# Revit family: 2CKA002064A0301
name_source: partatom
category: Elektroinstallationen
revit_build: Autodesk Revit 2017 (Build: 20160225_1515(x64)
units: mm (PartAtom-declared; Revit-internal decimal feet)

## family parameters
Basisbauteil = Fläche
Beim Laden mit Abzugskörper schneiden = Nein
Bemaßung runder Anschluss = Durchmesser verwenden
Beschriftungsausrichtung beibehalten = Ja
Gemeinsam genutzt = Nein
Raumberechnungspunkt = Nein
Teiletyp = Normal

## types (1)
- 2CKA002064A0301
    Abschließbar = Nein
    Anschlussart = Steckklemme
    Anzahl der Einheiten = 1
    Aufdruck/Kennzeichnung = ohne Aufdruck
    Ausführung = Schuko
    Ausführung der Oberfläche = glänzend
    Auswurfmechanismus = Nein
    BIM = https://media.live.bim.site
    BIMSITE_PRODUCT_ID = db384c0cd55333414ae2b7e2fc57784a7c25efdb
    Befestigungsart = Krallen-/Schraubbefestigung
    Beschreibung = SCHUKO Steckdosen-Einsatz, alpinweiß, Unterputz wassergeschützt, Sondersteckvorrichtungen, Steckdosen, SCHUKO Steckdosen-Einsatz mit Klappdeckel und Beschriftungsfeld Beschriftungsfeld 66,7 x 10 mm. Mit erhöhtem Berührungsschutz. Lieferumfang mit Dichtungsring. IP 44 nur in Verbindung mit Rahmen Allwetter 44. Mit Steckanschluss. 2-polig (2 P + E) Nennstrom: 16 A Schutzart Gerät: IP 44
    Datenblatt = https://media.live.bim.site
    Farbe = weiß
    Fehlerstromschutz = Nein
    GTIN = 4011395172322
    Geeignet für Schutzart (IP) = IP44
    Gerätebreite [mm] = 70
    Gerätehöhe [mm] = 131
    Gewicht [kg/m] = 0.097
    HAN = 2CKA002064A0301
    Halogenfrei = Ja
    HeinzeBIM = https://www.heinze.de
    Hersteller = Busch-Jaeger
    Ist System = Nein
    Ist Zubehör = Nein
    Metal = Metal
    Mit Klappdeckel = Ja
    Mit erhöhtem Berührungsschutz = Ja
    Montageart = Unterputz
    Nennspannung [V] [Volt] = 250
    Nennstrom = 16 A
    Oberfläche = unbehandelt
    Produktseite = https://media.live.bim.site
    RAL-Nummer (ähnlich) = 9010
    TYPE = 20 EUGKBN-34-101
    Textfeld/Beschriftungsfläche = Ja
    Typname = SCHUKO Steckdosen-Einsatz, alpinweiß, Unterputz wassergeschützt, Sondersteckvorrichtungen, Steckdosen
    URL = https://www.busch-jaeger.de
    Verdrehter Zentraleinsatz = Nein
    Vorgabe-Ansicht = 1219 mm
    Werkstoff = Kunststoff
    Werkstoffgüte = Thermoplast
    White = White
    Überspannungsschutz = Nein

## geometry (parser evidence)
native form markers: Sweep x5
no freeform markers — native parametric forms only
